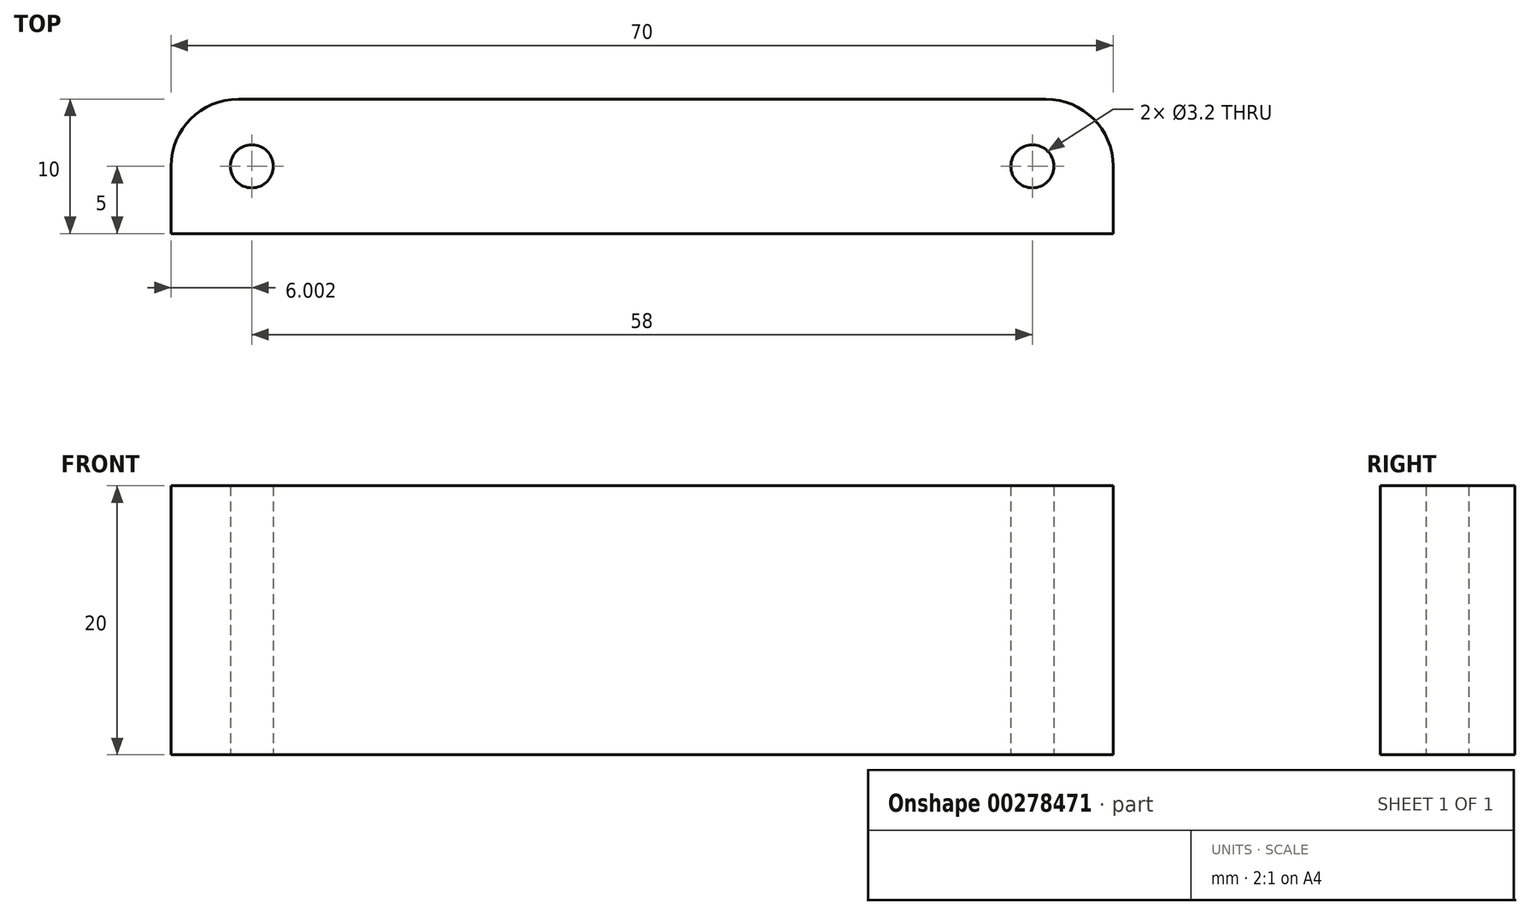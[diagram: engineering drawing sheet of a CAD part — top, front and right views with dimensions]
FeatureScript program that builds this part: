
annotation { "Feature Type Name" : "Feature", "Feature Type Description" : "" }
export const myFeature = defineFeature(function(context is Context, id is Id, definition is map)
    precondition{}
    {
        {
            var Q0;
            Q0=qCreatedBy(makeId("Top.planeOp"),FACE);
            var sketch = newSketch(context, id + "F0", { "sketchPlane" : qUnion([Q0])});
            skCircle(sketch, "E0", {"center": v(-33.28, 0) * mm, "radius": 1.6 * mm});
            skCircle(sketch, "E1", {"center": v(24.72, 0) * mm, "radius": 1.6 * mm});
            skLineSegment(sketch, "E2.bottom", {"start": v(-33.28, 5) * mm, "end": v(24.72, 5) * mm});
            skLineSegment(sketch, "E2.top", {"start": v(-33.28, -5) * mm, "end": v(24.72, -5) * mm});
            skLineSegment(sketch, "E2.left", {"start": v(-33.28, 5) * mm, "end": v(-33.28, -5) * mm, "construction": true});
            skLineSegment(sketch, "E2.right", {"start": v(24.72, 5) * mm, "end": v(24.72, -5) * mm, "construction": true});
            skLineSegment(sketch, "E3.bottom", {"start": v(-33.28, 5) * mm, "end": v(-39.28, 5) * mm});
            skLineSegment(sketch, "E3.top", {"start": v(-33.28, -5) * mm, "end": v(-39.28, -5) * mm});
            skLineSegment(sketch, "E3.right", {"start": v(-39.28, 5) * mm, "end": v(-39.28, -5) * mm});
            skLineSegment(sketch, "E4.bottom", {"start": v(24.72, 5) * mm, "end": v(30.72, 5) * mm});
            skLineSegment(sketch, "E4.top", {"start": v(24.72, -5) * mm, "end": v(30.72, -5) * mm});
            skLineSegment(sketch, "E4.right", {"start": v(30.72, 5) * mm, "end": v(30.72, -5) * mm});
            skSolve(sketch);
        }
        {
            var Q0;
            Q0=qSketchRegion(id+"F0",true);
            extrude(context, id + "F1", {"entities" : qUnion([Q0]), "depth" : 20 * mm});
        }
        {
            var Q0;
            Q0=makeQuery(id+"F1.opExtrude","SWEPT_EDGE",EDGE,{"disambiguationData":[OSD([sQuery(id+"F0.wireOp",EDGE,"E3.bottom"),sQuery(id+"F0.wireOp",EDGE,"E3.right")])]});
            var Q1;
            Q1=makeQuery(id+"F1.opExtrude","SWEPT_EDGE",EDGE,{"disambiguationData":[OSD([sQuery(id+"F0.wireOp",EDGE,"E4.bottom"),sQuery(id+"F0.wireOp",EDGE,"E4.right")])]});
            fillet(context, id + "F2", {"entities" : qUnion([Q0, Q1]), "radius" : 5 * mm, "tangentPropagation" : true, "allowEdgeOverflow" : false});
        }
    });
